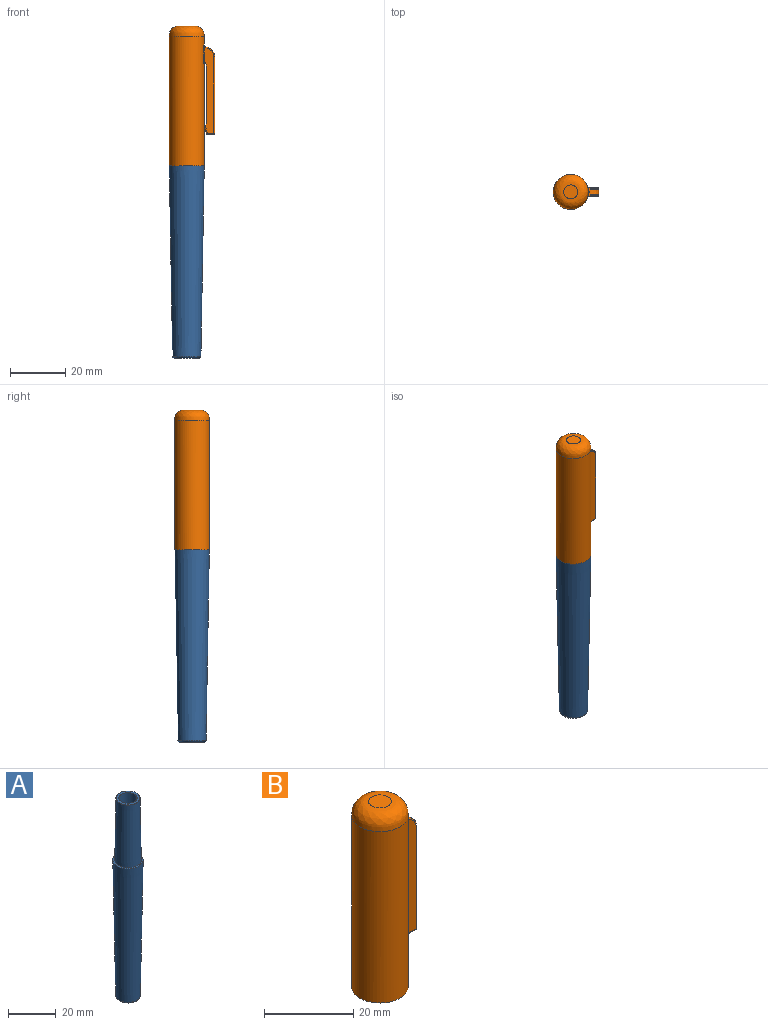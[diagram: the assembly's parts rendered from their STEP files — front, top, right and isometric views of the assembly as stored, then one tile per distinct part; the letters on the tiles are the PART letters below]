
ASSEMBLY  parts=2 mates=1
PART A: 10 faces, bbox 12.7x12.7x101.6 mm
  f0: cone r=5.56mm half-angle=1deg, axis (0,0,-1), area 1049.3mm2, adj f4,f5
  f1: cone r=6.35mm half-angle=1deg, axis (0,0,1), area 2499.6mm2, adj f3,f4
  f2: plane 9.01x9.01mm, normal (0,0,-1), area 63.8mm2, adj f3
  f3: torus R=4.51mm, axis (0,0,1), area 30.4mm2, adj f1,f2
  f4: plane 12.7x12.7mm, normal (0,0,1), area 29.7mm2, adj f0,f1
  f5: torus R=5mm, axis (0,0,1), area 6.3mm2, adj f0,f9
  f6: plane 6.35x6.35mm, normal (0,0,1), area 31.7mm2, adj f7
  f7: torus R=3.17mm, axis (0,0,1), area 22.4mm2, adj f6,f8
  f8: cylinder r=3.81mm len=97.16mm, axis (0,0,1), area 2325.8mm2, adj f7,f9
  f9: plane 10x10mm, normal (0,0,1), area 33mm2, adj f5,f8
PART B: 43 faces, bbox 16.9x12.8x50.9 mm
  f0: plane 0.35x0.06mm, normal (0,0,1), area 0mm2, adj f33,f34,f39
  f1: plane 31.19x3.53mm, normal (0,-1,0), area 84.3mm2, adj f11,f12,f17,f22,f27,f31,f34,f35
  f2: plane 31.2x3.54mm, normal (0,1,0), area 84.3mm2, adj f11,f12,f17,f18,f20,f25,f28,f32
  f3: plane 12.7x12.7mm, normal (0,0,-1), area 29.7mm2, adj f4,f7
  f4: cylinder r=6.35mm len=46.99mm, axis (0,0,-1), area 1851.9mm2, adj f3,f6,f30,f32,f33,f35,f36,f37
  f5: plane 5.09x5.09mm, normal (0,0,1), area 20.3mm2, adj f6
  f6: bspline ~12.7x12.7mm, area 196mm2, adj f4,f5
  f7: cylinder r=5.56mm len=31.75mm, axis (0,0,-1), area 1108.4mm2, adj f3,f8
  f8: plane 11.11x11.11mm, normal (0,0,-1), area 25.7mm2, adj f7,f10
  f9: plane 9.53x9.53mm, normal (0,0,-1), area 71.3mm2, adj f10
  f10: cylinder r=4.76mm len=15.88mm, axis (0,0,-1), area 475mm2, adj f8,f9
  f11: plane 20.7x3.18mm, normal (-1,0,0), area 65.4mm2, adj f1,f2,f12,f17
  f12: plane 3.25x0.91mm, normal (-0.69,0,0.72), area 3.6mm2, adj f1,f2,f11,f13,f18,f22
  f13: plane 2.74x2.54mm, normal (-0.96,0,-0.27), area 7.2mm2, adj f12,f18,f21,f22
  f14: plane 2.54x2.36mm, normal (0,0,-1), area 6mm2, adj f20,f21,f26,f27
  f15: plane 27.88x2.54mm, normal (1,0,0), area 70.8mm2, adj f25,f26,f31,f39,f40,f41
  f16: plane 0.35x0.06mm, normal (0,0,1), area 0mm2, adj f28,f33,f41
  f17: bspline ~6.06x2.67mm, area 5.3mm2, adj f1,f2,f11,f35
  f18: cylinder r=0.32mm len=2.98mm, axis (0.27,0,-0.96), area 1.5mm2, adj f2,f12,f13,f19
  f19: sphere r=0.32mm, area 0.2mm2, adj f18,f20,f21
  f20: cylinder r=0.32mm len=2.36mm, axis (1,0,0), area 1.2mm2, adj f2,f14,f19,f23
  f21: cylinder r=0.32mm len=2.54mm, axis (0,1,0), area 1mm2, adj f13,f14,f19,f24
  f22: cylinder r=0.32mm len=2.98mm, axis (-0.27,0,0.96), area 1.5mm2, adj f1,f12,f13,f24
  f23: sphere r=0.32mm, area 0.1mm2, adj f20,f25,f26
  f24: sphere r=0.32mm, area 0.1mm2, adj f21,f22,f27
  f25: cylinder r=0.32mm len=27.88mm, axis (0,0,1), area 13.9mm2, adj f2,f15,f23,f42
  f26: cylinder r=0.32mm len=2.54mm, axis (0,1,0), area 1.3mm2, adj f14,f15,f23,f29
  f27: cylinder r=0.32mm len=2.36mm, axis (-1,0,0), area 1.2mm2, adj f1,f14,f24,f29
  f28: cylinder r=0.32mm len=0.32mm, axis (-1,0,0), area 0.1mm2, adj f2,f16,f30,f42
  f29: sphere r=0.32mm, area 0.2mm2, adj f26,f27,f31
  f30: bspline ~0.76x0.74mm, area 0.3mm2, adj f4,f28,f32,f33
  f31: cylinder r=0.32mm len=27.88mm, axis (0,0,-1), area 13.9mm2, adj f1,f15,f29,f38
  f32: cylinder r=0.32mm len=5.6mm, axis (0,0,-1), area 2.2mm2, adj f2,f4,f30,f35
  f33: torus R=6.67mm, axis (0,0,1), area 1.2mm2, adj f0,f4,f16,f30,f36,f40
  f34: cylinder r=0.32mm len=0.32mm, axis (1,0,0), area 0.1mm2, adj f0,f1,f36,f38
  f35: bspline ~5.66x1.47mm, area 2.8mm2, adj f1,f2,f4,f17,f32,f37
  f36: bspline ~0.77x0.7mm, area 0.3mm2, adj f4,f33,f34,f37
  f37: cylinder r=0.32mm len=5.6mm, axis (0,0,-1), area 2.2mm2, adj f1,f4,f35,f36
  f38: torus R=3.24mm, axis (0,-1,0), area 2.7mm2, adj f1,f31,f34,f39
  f39: cylinder r=3.56mm len=3.56mm, axis (0,1,0), area 2mm2, adj f0,f15,f38,f40
  f40: bspline ~4.18x3.79mm, area 10.2mm2, adj f15,f33,f39,f41
  f41: cylinder r=3.56mm len=3.56mm, axis (0,1,0), area 2mm2, adj f15,f16,f40,f42
  f42: torus R=3.24mm, axis (0,-1,0), area 2.7mm2, adj f2,f25,f28,f41
PLACE A t=(19.13,5.14,16.63)mm fixed
PLACE B t=(19.13,5.14,10.28)mm
MATE slider B.f4 <-> A.f0  axis (0,0,-1) through (19.13,5.14,-15.12)mm
